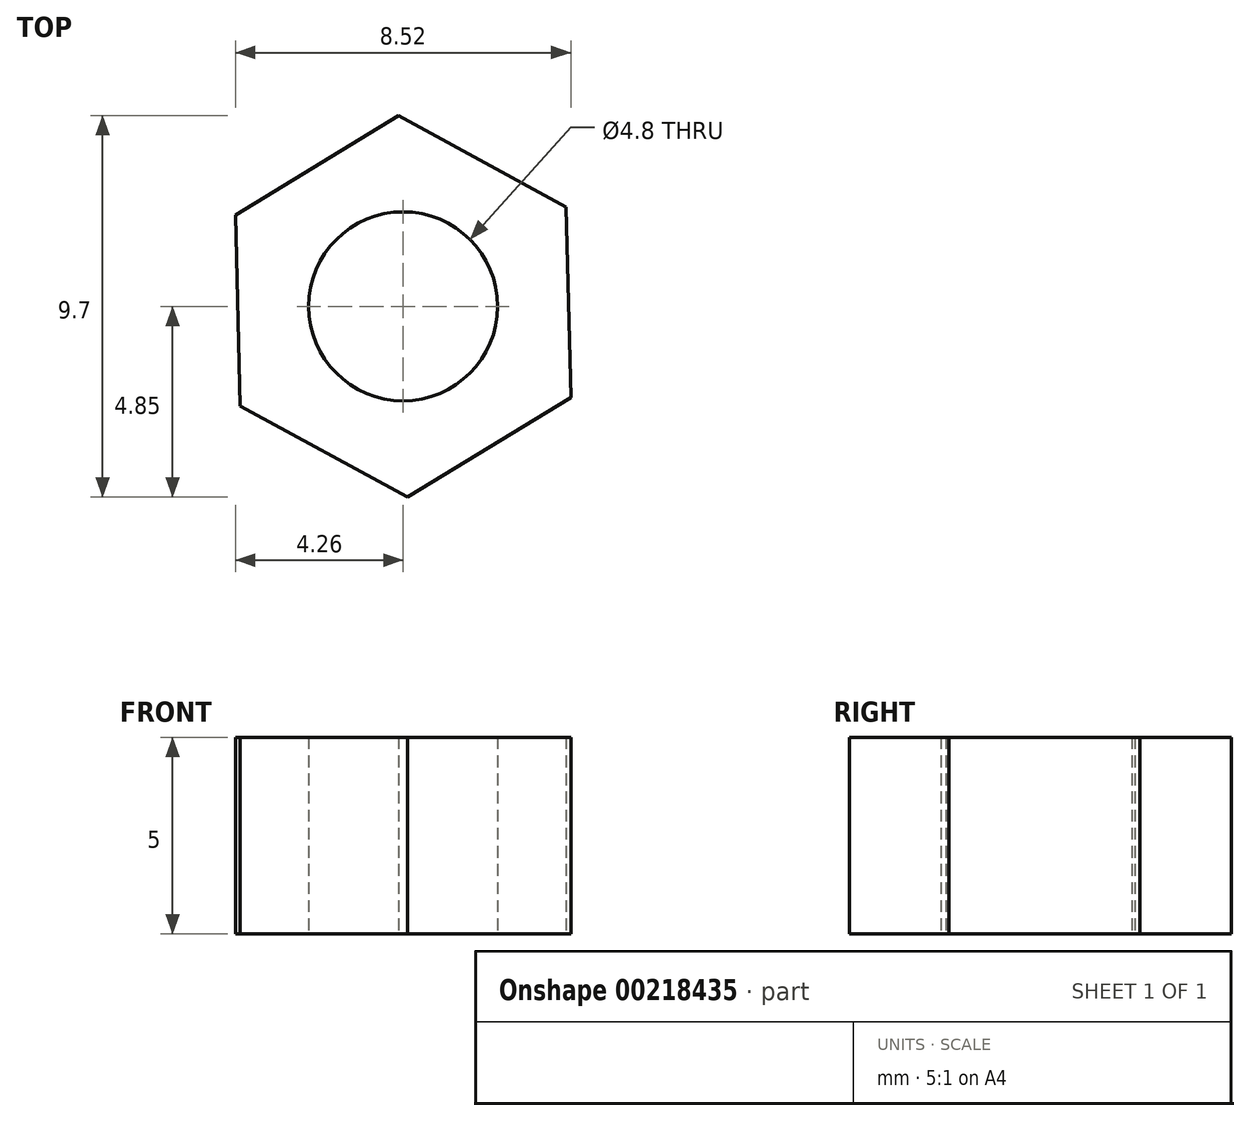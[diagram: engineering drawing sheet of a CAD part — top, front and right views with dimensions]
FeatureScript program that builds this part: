
annotation { "Feature Type Name" : "Feature", "Feature Type Description" : "" }
export const myFeature = defineFeature(function(context is Context, id is Id, definition is map)
    precondition{}
    {
        {
            var Q0;
            Q0=qCreatedBy(makeId("Top.planeOp"),FACE);
            var sketch = newSketch(context, id + "F0", { "sketchPlane" : qUnion([Q0])});
            skCircle(sketch, "E0", {"center": v(0, 0) * mm, "radius": 2.4 * mm});
            skCircle(sketch, "E1.cCircle", {"center": v(0, 0) * mm, "radius": 4.2 * mm, "construction": true});
            skLineSegment(sketch, "E1.0", {"start": v(-4.26, 2.32) * mm, "end": v(-0.12, 4.85) * mm});
            skLineSegment(sketch, "E1.1", {"start": v(-0.12, 4.85) * mm, "end": v(4.14, 2.53) * mm});
            skLineSegment(sketch, "E1.2", {"start": v(4.14, 2.53) * mm, "end": v(4.26, -2.32) * mm});
            skLineSegment(sketch, "E1.3", {"start": v(4.26, -2.32) * mm, "end": v(0.12, -4.85) * mm});
            skLineSegment(sketch, "E1.4", {"start": v(0.12, -4.85) * mm, "end": v(-4.14, -2.53) * mm});
            skLineSegment(sketch, "E1.5", {"start": v(-4.14, -2.53) * mm, "end": v(-4.26, 2.32) * mm});
            skPoint(sketch, "E1.0.midPoint", {"position": v(-2.19, 3.59) * mm});
            skSolve(sketch);
        }
        {
            var Q0;
            Q0=makeQuery(id+"F0.imprint","IMPRINT",FACE,{"disambiguationData":[TD([[makeQuery(id+"F0.imprint","IMPRINT",EDGE,{"derivedFrom":sQuery(id+"F0.wireOp",EDGE,"E0")}),-1.0]])]});
            extrude(context, id + "F1", {"entities" : qUnion([Q0]), "depth" : 5 * mm});
        }
    });
